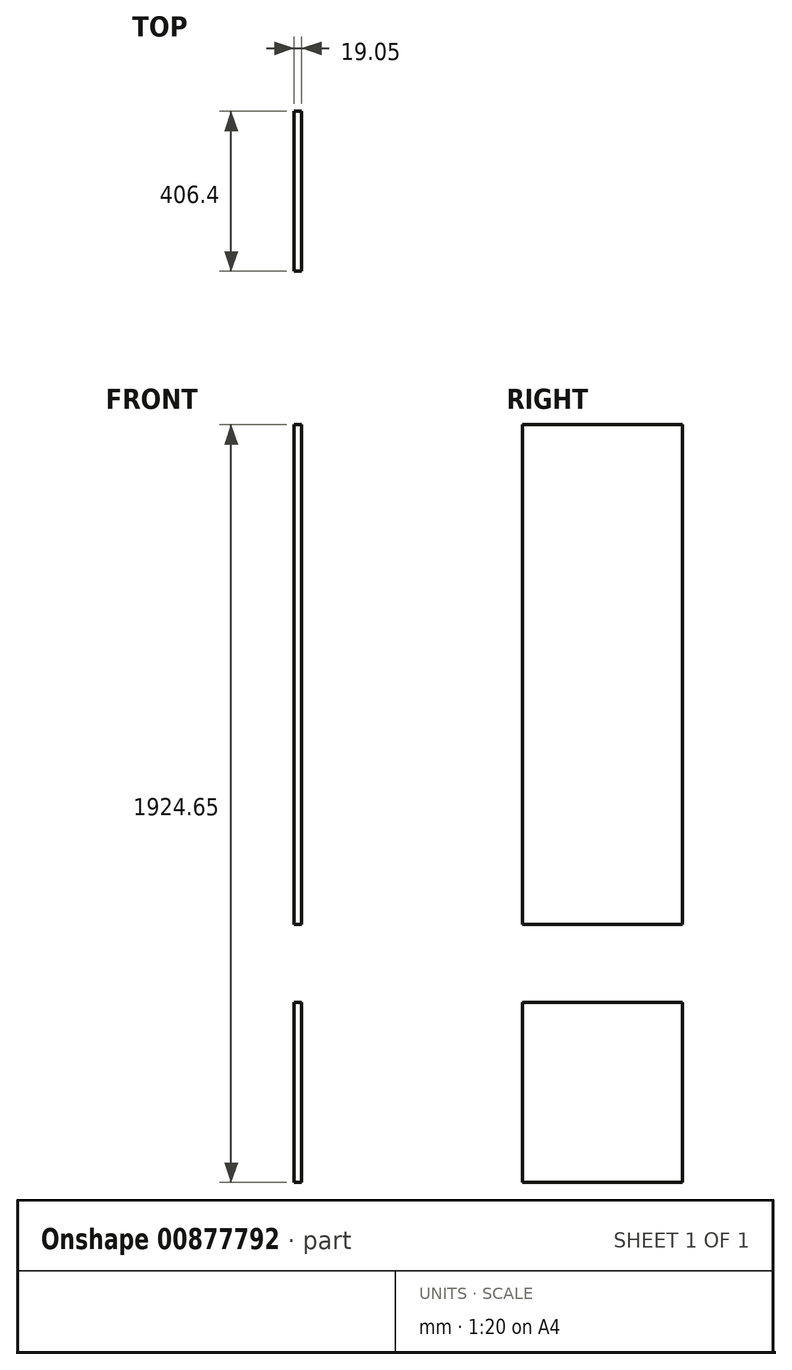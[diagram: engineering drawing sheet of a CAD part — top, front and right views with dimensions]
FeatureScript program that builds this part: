
annotation { "Feature Type Name" : "Feature", "Feature Type Description" : "" }
export const myFeature = defineFeature(function(context is Context, id is Id, definition is map)
    precondition{}
    {
        {
            var Q0;
            Q0=qCreatedBy(makeId("Right.planeOp"),FACE);
            var sketch = newSketch(context, id + "F0", { "sketchPlane" : qUnion([Q0])});
            skLineSegment(sketch, "E0.bottom", {"start": v(-218.7, 1379.5) * mm, "end": v(187.7, 1379.5) * mm});
            skLineSegment(sketch, "E0.top", {"start": v(-218.7, -373.1) * mm, "end": v(187.7, -373.1) * mm});
            skLineSegment(sketch, "E0.left", {"start": v(-218.7, 1379.5) * mm, "end": v(-218.7, -373.1) * mm});
            skLineSegment(sketch, "E0.right", {"start": v(187.7, 1379.5) * mm, "end": v(187.7, -373.1) * mm});
            skLineSegment(sketch, "E1.bottom", {"start": v(577.44, 69.41) * mm, "end": v(983.84, 69.41) * mm});
            skLineSegment(sketch, "E1.top", {"start": v(577.44, -387.79) * mm, "end": v(983.84, -387.79) * mm});
            skLineSegment(sketch, "E1.left", {"start": v(577.44, 69.41) * mm, "end": v(577.44, -387.79) * mm});
            skLineSegment(sketch, "E1.right", {"start": v(983.84, 69.41) * mm, "end": v(983.84, -387.79) * mm});
            skLineSegment(sketch, "E2.bottom", {"start": v(577.44, 1536.86) * mm, "end": v(983.84, 1536.86) * mm});
            skLineSegment(sketch, "E2.top", {"start": v(577.44, 266.86) * mm, "end": v(983.84, 266.86) * mm});
            skLineSegment(sketch, "E2.left", {"start": v(577.44, 1536.86) * mm, "end": v(577.44, 266.86) * mm});
            skLineSegment(sketch, "E2.right", {"start": v(983.84, 1536.86) * mm, "end": v(983.84, 266.86) * mm});
            skSolve(sketch);
        }
        {
            var Q0;
            Q0=makeQuery(id+"F0.imprint","IMPRINT",FACE,{"disambiguationData":[TD([[makeQuery(id+"F0.imprint","IMPRINT",EDGE,{"derivedFrom":sQuery(id+"F0.wireOp",EDGE,"E1.bottom")}),-1.0]])]});
            var Q1;
            Q1=makeQuery(id+"F0.imprint","IMPRINT",FACE,{"disambiguationData":[TD([[makeQuery(id+"F0.imprint","IMPRINT",EDGE,{"derivedFrom":sQuery(id+"F0.wireOp",EDGE,"E2.bottom")}),-1.0]])]});
            extrude(context, id + "F1", {"entities" : qUnion([Q0, Q1]), "depth" : 19.05 * mm, "offsetDistance" : 25.4 * mm});
        }
    });
